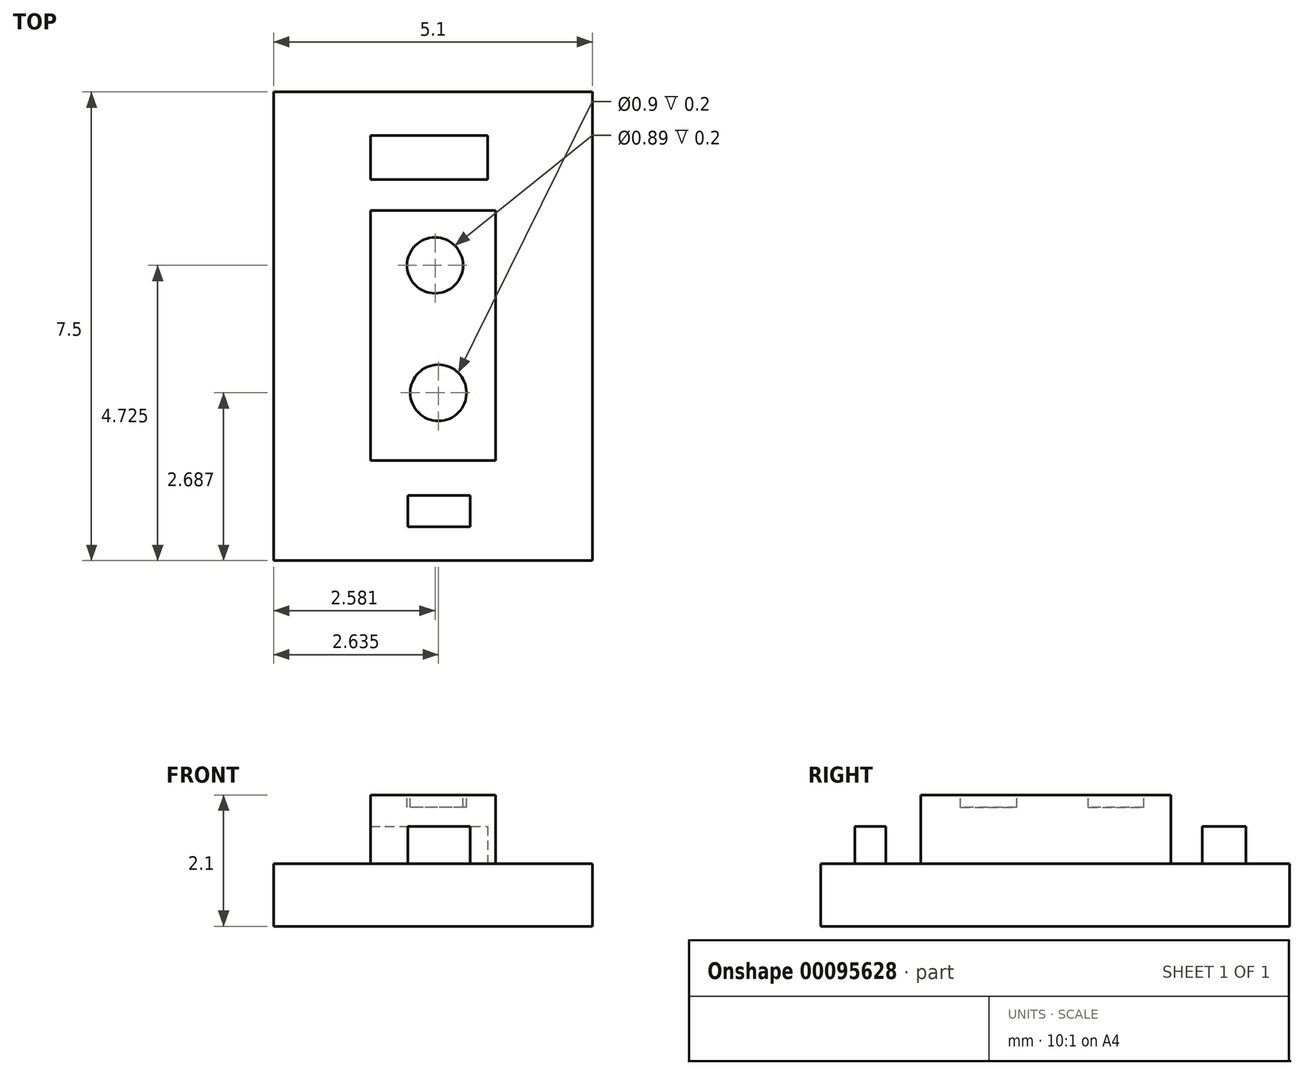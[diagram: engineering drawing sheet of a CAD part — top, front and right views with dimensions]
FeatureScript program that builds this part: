
annotation { "Feature Type Name" : "Feature", "Feature Type Description" : "" }
export const myFeature = defineFeature(function(context is Context, id is Id, definition is map)
    precondition{}
    {
        {
            var Q0;
            Q0=qCreatedBy(makeId("Top.planeOp"),FACE);
            var sketch = newSketch(context, id + "F0", { "sketchPlane" : qUnion([Q0])});
            skLineSegment(sketch, "E0.bottom", {"start": v(0, 0) * mm, "end": v(2, 0) * mm});
            skLineSegment(sketch, "E0.top", {"start": v(0, 4) * mm, "end": v(2, 4) * mm});
            skLineSegment(sketch, "E0.left", {"start": v(0, 0) * mm, "end": v(0, 4) * mm});
            skLineSegment(sketch, "E0.right", {"start": v(2, 0) * mm, "end": v(2, 4) * mm});
            skSolve(sketch);
        }
        {
            var Q0;
            Q0=qSketchRegion(id+"F0",true);
            extrude(context, id + "F1", {"entities" : qUnion([Q0]), "depth" : 1.1 * mm});
        }
        {
            var Q0;
            Q0=makeQuery(id+"F1.opExtrude","CAP_FACE",FACE,{"disambiguationData":[OSD([sQuery(id+"F0.wireOp",EDGE,"E0.bottom"),sQuery(id+"F0.wireOp",EDGE,"E0.top"),sQuery(id+"F0.wireOp",EDGE,"E0.left"),sQuery(id+"F0.wireOp",EDGE,"E0.right")])],"isStart":true});
            var sketch = newSketch(context, id + "F2", { "sketchPlane" : qUnion([Q0])});
            skLineSegment(sketch, "E1.bottom", {"start": v(-1.55, 1.6) * mm, "end": v(3.55, 1.6) * mm});
            skLineSegment(sketch, "E1.top", {"start": v(-1.55, -5.9) * mm, "end": v(3.55, -5.9) * mm});
            skLineSegment(sketch, "E1.left", {"start": v(-1.55, 1.6) * mm, "end": v(-1.55, -5.9) * mm});
            skLineSegment(sketch, "E1.right", {"start": v(3.55, 1.6) * mm, "end": v(3.55, -5.9) * mm});
            skSolve(sketch);
        }
        {
            var Q0;
            Q0=makeQuery(id+"F2.imprint","IMPRINT",FACE,{"disambiguationData":[TD([[makeQuery(id+"F2.imprint","IMPRINT",EDGE,{"derivedFrom":sQuery(id+"F2.wireOp",EDGE,"E1.bottom")}),-1.0]])]});
            var Q1;
            Q1=makeQuery(id+"F2.imprint","IMPRINT",FACE,{"disambiguationData":[TD([[makeQuery(id+"F2.imprint","IMPRINT",EDGE,{"derivedFrom":makeQuery(id+"F1.opExtrude","CAP_EDGE",EDGE,{"disambiguationData":[OSD([sQuery(id+"F0.wireOp",EDGE,"E0.bottom")])],"isStart":true})}),-1.0]])]});
            extrude(context, id + "F3", {"entities" : qUnion([Q0, Q1]), "depth" : 1 * mm});
        }
        {
            var Q0;
            Q0=makeQuery(id+"F3.opExtrude","CAP_FACE",FACE,{"disambiguationData":[OSD([sQuery(id+"F2.wireOp",EDGE,"E1.bottom"),sQuery(id+"F2.wireOp",EDGE,"E1.top"),sQuery(id+"F2.wireOp",EDGE,"E1.left"),sQuery(id+"F2.wireOp",EDGE,"E1.right")])],"isStart":true});
            var sketch = newSketch(context, id + "F4", { "sketchPlane" : qUnion([Q0])});
            skLineSegment(sketch, "E2.bottom", {"start": v(0.6, -0.56) * mm, "end": v(1.6, -0.56) * mm});
            skLineSegment(sketch, "E2.top", {"start": v(0.6, -1.06) * mm, "end": v(1.6, -1.06) * mm});
            skLineSegment(sketch, "E2.left", {"start": v(0.6, -0.56) * mm, "end": v(0.6, -1.06) * mm});
            skLineSegment(sketch, "E2.right", {"start": v(1.6, -0.56) * mm, "end": v(1.6, -1.06) * mm});
            skSolve(sketch);
        }
        {
            var Q0;
            Q0=qSketchRegion(id+"F4",true);
            extrude(context, id + "F5", {"entities" : qUnion([Q0]), "depth" : .6 * mm});
        }
        {
            var Q0;
            Q0=makeQuery(id+"F3.opExtrude","CAP_FACE",FACE,{"disambiguationData":[OSD([sQuery(id+"F2.wireOp",EDGE,"E1.bottom"),sQuery(id+"F2.wireOp",EDGE,"E1.top"),sQuery(id+"F2.wireOp",EDGE,"E1.left"),sQuery(id+"F2.wireOp",EDGE,"E1.right")])],"isStart":true});
            var sketch = newSketch(context, id + "F6", { "sketchPlane" : qUnion([Q0])});
            skLineSegment(sketch, "E3.bottom", {"start": v(0, 5.2) * mm, "end": v(1.87, 5.2) * mm});
            skLineSegment(sketch, "E3.top", {"start": v(0, 4.5) * mm, "end": v(1.87, 4.5) * mm});
            skLineSegment(sketch, "E3.left", {"start": v(0, 5.2) * mm, "end": v(0, 4.5) * mm});
            skLineSegment(sketch, "E3.right", {"start": v(1.87, 5.2) * mm, "end": v(1.87, 4.5) * mm});
            skSolve(sketch);
        }
        {
            var Q0;
            Q0=qSketchRegion(id+"F6",true);
            extrude(context, id + "F7", {"entities" : qUnion([Q0]), "depth" : .6 * mm});
        }
        {
            var Q0;
            Q0=makeQuery(id+"F1.opExtrude","CAP_FACE",FACE,{"disambiguationData":[OSD([sQuery(id+"F0.wireOp",EDGE,"E0.bottom"),sQuery(id+"F0.wireOp",EDGE,"E0.top"),sQuery(id+"F0.wireOp",EDGE,"E0.left"),sQuery(id+"F0.wireOp",EDGE,"E0.right")])],"isStart":false});
            var sketch = newSketch(context, id + "F8", { "sketchPlane" : qUnion([Q0])});
            skCircle(sketch, "E4", {"center": v(1.03, 3.12) * mm, "radius": 0.45 * mm});
            skCircle(sketch, "E5", {"center": v(1.08, 1.09) * mm, "radius": 0.45 * mm});
            skSolve(sketch);
        }
        {
            var Q0;
            Q0=makeQuery(id+"F8.imprint","IMPRINT",FACE,{"disambiguationData":[TD([[makeQuery(id+"F8.imprint","IMPRINT",EDGE,{"derivedFrom":sQuery(id+"F8.wireOp",EDGE,"E4")}),1.0]])]});
            var Q1;
            Q1=makeQuery(id+"F8.imprint","IMPRINT",FACE,{"disambiguationData":[TD([[makeQuery(id+"F8.imprint","IMPRINT",EDGE,{"derivedFrom":sQuery(id+"F8.wireOp",EDGE,"E5")}),1.0]])]});
            extrude(context, id + "F9", {"entities" : qUnion([Q0, Q1]), "operationType" : NewBodyOperationType.REMOVE, "oppositeDirection" : true, "depth" : .2 * mm});
        }
    });
